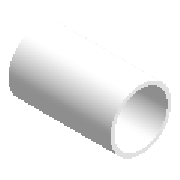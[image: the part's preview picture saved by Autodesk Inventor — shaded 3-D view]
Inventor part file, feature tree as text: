
AUTODESK INVENTOR PART (.ipt)
format: ipt  version: 2023 (Build 270158000, 158)  size: 157,184 bytes
history: native  units: mm (DEFAULTED — no unit token found)
features: other x6, revolve x1, sketch x1
ambient origin geometry x8: Origin, YZ Plane, XZ Plane, XY Plane, X Axis, Y Axis, Z Axis, Center Point
bodies: Solid1 (feature_tree)
feature tree (8):
  revolve  "Revolution1"  [1 undecoded]
  other  "Work Point1"
  other  "Work Point2"
  other  "Work Axis1"
  other  "Work Point3"
  other  "Work Axis2"
  other  "Work Point4"
  sketch  "Sketch1"  dims[d1=110.0mm d0=110.0mm d2=8.2mm d3=6.0mm d4=61.0mm d5=8.2mm d7=90.0deg]
note: 1 required parameter value undecoded (feature->parameter linkage not recoverable at this tier; creation-order binding heuristic only, values carry confidence <= 0.55)
